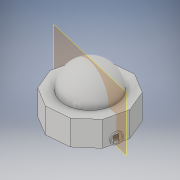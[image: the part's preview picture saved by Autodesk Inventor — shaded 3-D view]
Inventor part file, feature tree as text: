
AUTODESK INVENTOR PART (.ipt)
format: ipt  version: 2017 (Build 210142000, 142)  size: 271,360 bytes
history: native  units: in
note: dims shown in document units (in); Inventor stores cm internally (conversion verified against a paired STEP export)
features: sketch x7, extrude x6, other x2, plane x2, mirror x1
ambient origin geometry x8: Origin, YZ Plane, XZ Plane, XY Plane, X Axis, Y Axis, Z Axis, Center Point
bodies: Solid1 (feature_tree)
feature tree (18):
  other  "dome"
  extrude  "bace"  Depth=1.0in TaperAngle=0.0deg
  extrude  "bace wall"  Depth=20.0in TaperAngle=0.0deg
  extrude  "bace cieiling"  Depth=1.0in TaperAngle=0.0deg
  plane  "Work Plane1"
  extrude  "door frame"  TaperAngle=90.0deg  [1 undecoded]
  extrude  "corridor connection"  Depth=2.0in
  extrude  "left door slot"  Depth=1.0in TaperAngle=0.0deg
  other  "door slot mirror"
  mirror  "Mirror1"
  plane  "Work Plane3"
  sketch  "Sketch1"  dims[d0=62.0in d1=1.0in d2=0.0in]
  sketch  "Sketch2"  dims[d4=1.0in d5=20.0in d6=0.0in]
  sketch  "Sketch3"  dims[d7=40.0in d8=1.0in d9=0.0in]
  sketch  "Sketch6"  dims[d12=1.0in d13=90.0deg]
  sketch  "Sketch7"  dims[d14=6.6667in d15=4.0in d16=2.0in d17=6.6667in]
  sketch  "Sketch8"  dims[d18=1.0in d19=0.0in d20=1.0in d21=0.0in]
  sketch  "Sketch9"  dims[d22=0.25in d23=0.5in d24=6.6667in d25=2.0in d26=0.0in]
note: 1 required parameter value undecoded (feature->parameter linkage not recoverable at this tier; creation-order binding heuristic only, values carry confidence <= 0.55)
